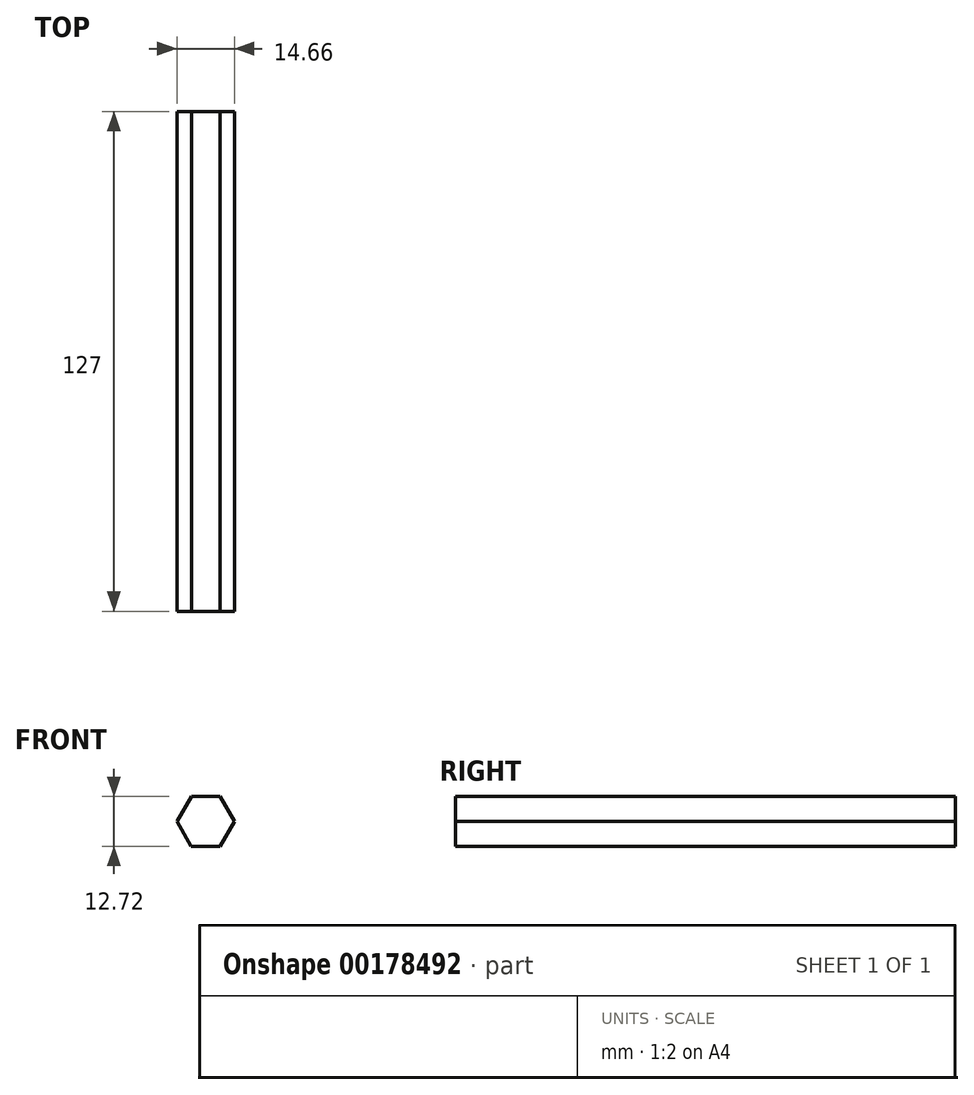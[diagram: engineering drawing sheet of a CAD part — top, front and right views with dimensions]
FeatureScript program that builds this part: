
annotation { "Feature Type Name" : "Feature", "Feature Type Description" : "" }
export const myFeature = defineFeature(function(context is Context, id is Id, definition is map)
    precondition{}
    {
        {
            var Q0;
            Q0=qCreatedBy(makeId("Front.planeOp"),FACE);
            var sketch = newSketch(context, id + "F0", { "sketchPlane" : qUnion([Q0])});
            skCircle(sketch, "E0", {"center": v(0, 0) * mm, "radius": 6.35 * mm});
            skCircle(sketch, "E1.cCircle", {"center": v(0, 0) * mm, "radius": 6.35 * mm, "construction": true});
            skLineSegment(sketch, "E1.0", {"start": v(7.33, -0.03) * mm, "end": v(3.64, -6.36) * mm});
            skLineSegment(sketch, "E1.1", {"start": v(3.64, -6.36) * mm, "end": v(-3.7, -6.34) * mm});
            skLineSegment(sketch, "E1.2", {"start": v(-3.7, -6.34) * mm, "end": v(-7.33, 0.03) * mm});
            skLineSegment(sketch, "E1.3", {"start": v(-7.33, 0.03) * mm, "end": v(-3.64, 6.36) * mm});
            skLineSegment(sketch, "E1.4", {"start": v(-3.64, 6.36) * mm, "end": v(3.7, 6.34) * mm});
            skLineSegment(sketch, "E1.5", {"start": v(3.7, 6.34) * mm, "end": v(7.33, -0.03) * mm});
            skPoint(sketch, "E1.0.midPoint", {"position": v(5.49, -3.2) * mm});
            skSolve(sketch);
        }
        {
            var Q0;
            Q0 = qSketchRegion(id + "F0", true);
            extrude(context, id + "F1", {"entities" : qUnion([Q0]), "depth" : 127 * mm});
        }
    });
